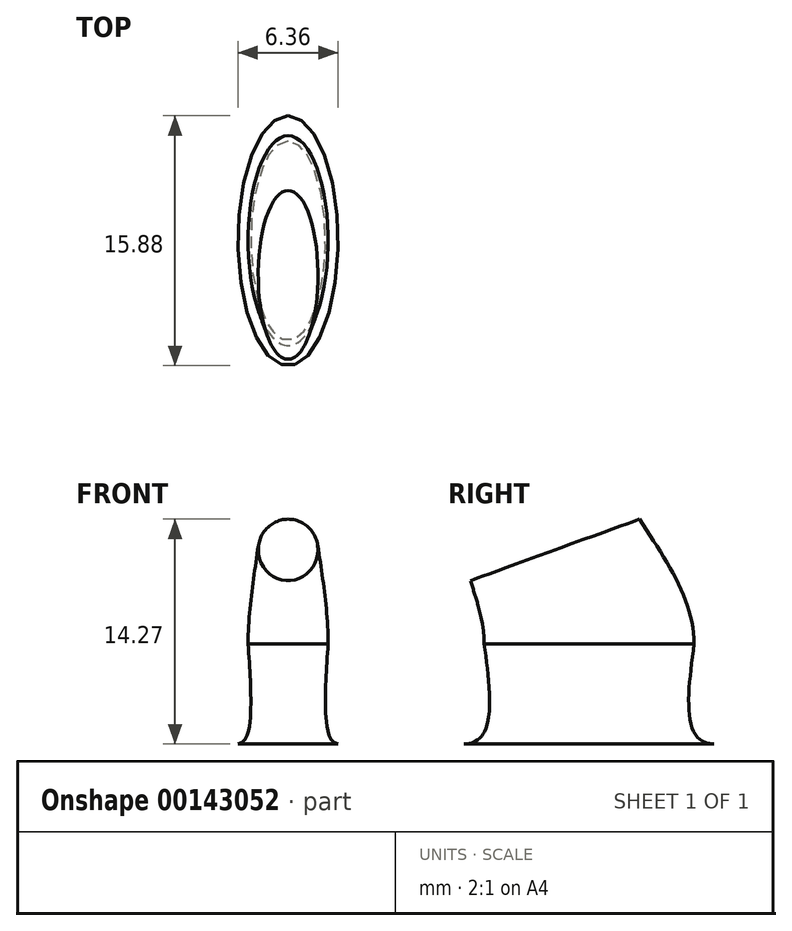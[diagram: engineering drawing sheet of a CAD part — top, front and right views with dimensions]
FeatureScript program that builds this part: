
annotation { "Feature Type Name" : "Feature", "Feature Type Description" : "" }
export const myFeature = defineFeature(function(context is Context, id is Id, definition is map)
    precondition{}
    {
        {
            var Q0;
            Q0=qCreatedBy(makeId("Top.planeOp"),FACE);
            var sketch = newSketch(context, id + "F0", { "sketchPlane" : qUnion([Q0])});
            skEllipse(sketch, "E0", {"center": v(0, 0) * mm, "majorRadius": 7.94 * mm, "minorRadius": 3.18 * mm, "majorAxis": v(0, 1)});
            skLineSegment(sketch, "E1", {"start": v(-3.18, 0) * mm, "end": v(3.18, 0) * mm, "construction": true});
            skSolve(sketch);
        }
        {
            var Q0;
            Q0=qCreatedBy(makeId("Top.planeOp"),FACE);
            cPlane(context, id + "F1", {"entities" : qUnion([Q0]), "cplaneType" : CPlaneType.OFFSET, "offset" : 6.35 * mm, "width" : 152.4 * mm, "height" : 152.4 * mm});
        }
        {
            var Q0;
            Q0=qCreatedBy(id+"F1.planeOp",FACE);
            var sketch = newSketch(context, id + "F2", { "sketchPlane" : qUnion([Q0])});
            skEllipse(sketch, "E2", {"center": v(0, 0) * mm, "majorRadius": 6.67 * mm, "minorRadius": 2.54 * mm, "majorAxis": v(0, 1)});
            skLineSegment(sketch, "E3", {"start": v(-2.54, 0) * mm, "end": v(2.54, 0) * mm, "construction": true});
            skSolve(sketch);
        }
        {
            var Q0;
            Q0=makeQuery(id+"F0.imprint","IMPRINT",FACE,{"disambiguationData":[TD([[makeQuery(id+"F0.imprint","IMPRINT",EDGE,{"derivedFrom":sQuery(id+"F0.wireOp",EDGE,"E0")}),1.0]])]});
            var Q1;
            Q1=makeQuery(id+"F2.imprint","IMPRINT",FACE,{"disambiguationData":[TD([[makeQuery(id+"F2.imprint","IMPRINT",EDGE,{"derivedFrom":sQuery(id+"F2.wireOp",EDGE,"E2")}),1.0]])]});
            loft(context, id + "F3", {"startCondition" : LoftEndDerivativeType.TANGENT_TO_PROFILE, "startMagnitude" : 5, "sheetProfilesArray" : [{ "sheetProfileEntities" : qUnion([Q0]) }, { "sheetProfileEntities" : qUnion([Q1]) }]});
        }
        {
            var Q0;
            Q0=sQuery(id+"F2.wireOp",EDGE,"E3");
            var Q1;
            Q1=makeQuery(id+"F2.imprint","IMPRINT",FACE,{"disambiguationData":[TD([[makeQuery(id+"F2.imprint","IMPRINT",EDGE,{"derivedFrom":sQuery(id+"F2.wireOp",EDGE,"E2")}),1.0]])]});
            cPlane(context, id + "F4", {"entities" : qUnion([Q0, Q1]), "cplaneType" : CPlaneType.LINE_ANGLE, "offset" : 25.4 * mm, "angle" : 20 * degree, "width" : 152.4 * mm, "height" : 152.4 * mm});
        }
        {
            var Q0;
            Q0=qCreatedBy(id+"F4.planeOp",FACE);
            cPlane(context, id + "F5", {"entities" : qUnion([Q0]), "cplaneType" : CPlaneType.OFFSET, "offset" : 6.35 * mm, "oppositeDirection" : true, "width" : 152.4 * mm, "height" : 152.4 * mm});
        }
        {
            var Q0;
            Q0=qCreatedBy(id+"F5.planeOp",FACE);
            var sketch = newSketch(context, id + "F6", { "sketchPlane" : qUnion([Q0])});
            skEllipse(sketch, "E4", {"center": v(0, -2.17) * mm, "majorRadius": 5.72 * mm, "minorRadius": 1.9 * mm, "majorAxis": v(0, -1)});
            skLineSegment(sketch, "E5", {"start": v(-1.9, -2.17) * mm, "end": v(1.9, -2.17) * mm, "construction": true});
            skSolve(sketch);
        }
        {
            var Q0;
            Q0 = qSketchRegion(id + "F2", true);
            var Q1;
            Q1 = qSketchRegion(id + "F6", true);
            loft(context, id + "F7", {"operationType" : NewBodyOperationType.ADD, "startCondition" : LoftEndDerivativeType.NORMAL_TO_PROFILE, "startMagnitude" : 1, "sheetProfilesArray" : [{ "sheetProfileEntities" : qUnion([Q0]) }, { "sheetProfileEntities" : qUnion([Q1]) }]});
        }
        {
            var Q0;
            Q0=sQuery(id+"F6.wireOp",EDGE,"E5");
            var Q1;
            Q1=qCreatedBy(id+"F5.planeOp",FACE);
            cPlane(context, id + "F8", {"entities" : qUnion([Q0, Q1]), "cplaneType" : CPlaneType.LINE_ANGLE, "offset" : 25.4 * mm, "angle" : 20 * degree, "width" : 152.4 * mm, "height" : 152.4 * mm});
        }
    });
